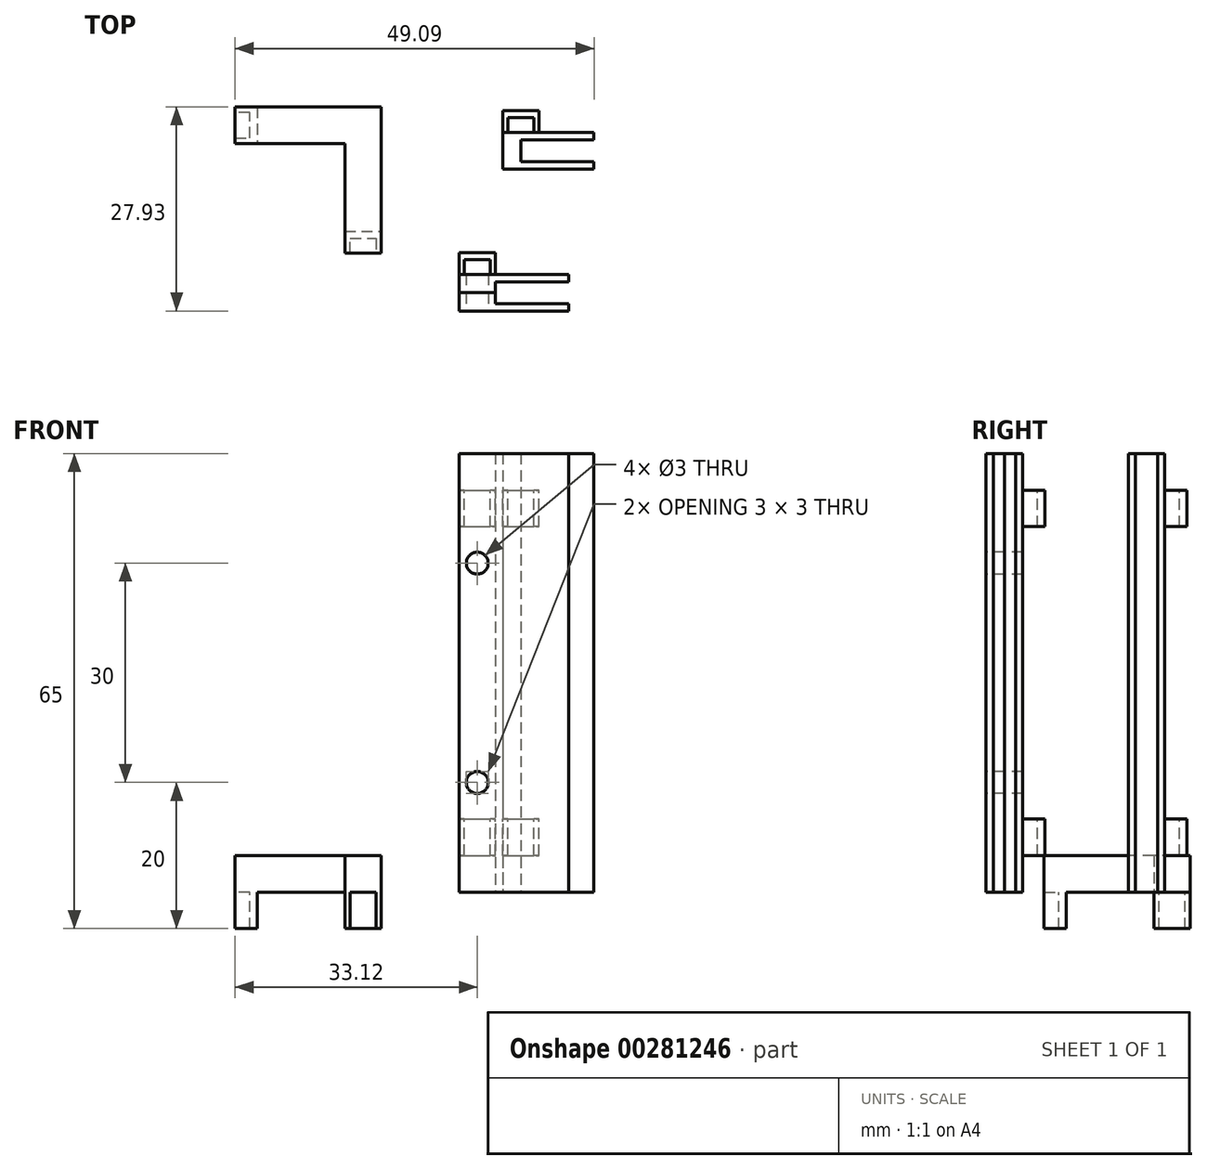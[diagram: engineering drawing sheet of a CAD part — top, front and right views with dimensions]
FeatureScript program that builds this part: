
annotation { "Feature Type Name" : "Feature", "Feature Type Description" : "" }
export const myFeature = defineFeature(function(context is Context, id is Id, definition is map)
    precondition{}
    {
        {
            var Q0;
            Q0=qCreatedBy(makeId("Top.planeOp"),FACE);
            var sketch = newSketch(context, id + "F0", { "sketchPlane" : qUnion([Q0])});
            skLineSegment(sketch, "E0.bottom", {"start": v(0, 0) * mm, "end": v(-10, 0) * mm});
            skLineSegment(sketch, "E0.top", {"start": v(0, 3) * mm, "end": v(-10, 3) * mm});
            skLineSegment(sketch, "E0.left", {"start": v(0, 0) * mm, "end": v(0, 3) * mm});
            skLineSegment(sketch, "E0.right", {"start": v(-10, 0) * mm, "end": v(-10, 3) * mm});
            skLineSegment(sketch, "E1.bottom", {"start": v(0, 0) * mm, "end": v(-15, 0) * mm});
            skLineSegment(sketch, "E1.top", {"start": v(0, -1) * mm, "end": v(-15, -1) * mm});
            skLineSegment(sketch, "E1.left", {"start": v(0, 0) * mm, "end": v(0, -1) * mm});
            skLineSegment(sketch, "E1.right", {"start": v(-15, 0) * mm, "end": v(-15, -1) * mm});
            skLineSegment(sketch, "E2.bottom", {"start": v(0, 3) * mm, "end": v(-15, 3) * mm});
            skLineSegment(sketch, "E2.top", {"start": v(0, 4) * mm, "end": v(-15, 4) * mm});
            skLineSegment(sketch, "E2.left", {"start": v(0, 3) * mm, "end": v(0, 4) * mm});
            skLineSegment(sketch, "E2.right", {"start": v(-15, 3) * mm, "end": v(-15, 4) * mm});
            skLineSegment(sketch, "E3", {"start": v(-15, 3) * mm, "end": v(-15, 0) * mm});
            skLineSegment(sketch, "E4", {"start": v(-15, 1.5) * mm, "end": v(-10, 1.5) * mm});
            skSolve(sketch);
        }
        {
            var Q0;
            Q0=makeQuery(id+"F0.imprint","IMPRINT",FACE,{"disambiguationData":[TD([[makeQuery(id+"F0.imprint","IMPRINT",EDGE,{"derivedFrom":sQuery(id+"F0.wireOp",EDGE,"E2.top")}),1.0]])]});
            var Q1;
            {var subQ3=sQuery(id+"F0.wireOp",EDGE,"E4");Q1=makeQuery(id+"F0.imprint","IMPRINT",FACE,{"disambiguationData":[TD([[makeQuery(id+"F0.imprint","IMPRINT",EDGE,{"derivedFrom":subQ3}),1.0]])]});}
            extrude(context, id + "F1", {"entities" : qUnion([Q0, Q1]), "depth" : 60 * mm});
        }
        {
            var Q0;
            {var subQ3=sQuery(id+"F0.wireOp",EDGE,"E4");Q0=makeQuery(id+"F0.imprint","IMPRINT",FACE,{"disambiguationData":[TD([[makeQuery(id+"F0.imprint","IMPRINT",EDGE,{"derivedFrom":subQ3}),-1.0]])]});}
            var Q1;
            Q1=makeQuery(id+"F0.imprint","IMPRINT",FACE,{"disambiguationData":[TD([[makeQuery(id+"F0.imprint","IMPRINT",EDGE,{"derivedFrom":sQuery(id+"F0.wireOp",EDGE,"E1.top")}),-1.0]])]});
            extrude(context, id + "F2", {"entities" : qUnion([Q0, Q1]), "depth" : 60 * mm});
        }
        {
            var Q0;
            Q0=makeQuery(id+"F2.opExtrude","SWEPT_FACE",FACE,{"disambiguationData":[OSD([sQuery(id+"F0.wireOp",EDGE,"E1.top")])]});
            var sketch = newSketch(context, id + "F3", { "sketchPlane" : qUnion([Q0])});
            skLineSegment(sketch, "E5.bottom", {"start": v(-15, 60) * mm, "end": v(-10, 60) * mm});
            skLineSegment(sketch, "E5.top", {"start": v(-15, 0) * mm, "end": v(-10, 0) * mm});
            skLineSegment(sketch, "E5.left", {"start": v(-15, 60) * mm, "end": v(-15, 0) * mm});
            skLineSegment(sketch, "E5.right", {"start": v(-10, 60) * mm, "end": v(-10, 0) * mm});
            skLineSegment(sketch, "E6.bottom", {"start": v(-15, 30) * mm, "end": v(-10, 30) * mm});
            skLineSegment(sketch, "E6.left", {"start": v(-15, 30) * mm, "end": v(-15, 60) * mm});
            skLineSegment(sketch, "E6.right", {"start": v(-10, 30) * mm, "end": v(-10, 60) * mm});
            skLineSegment(sketch, "E7.left", {"start": v(-15, 30) * mm, "end": v(-15, 0) * mm});
            skLineSegment(sketch, "E7.right", {"start": v(-10, 30) * mm, "end": v(-10, 0) * mm});
            skCircle(sketch, "E8", {"center": v(-12.5, 15) * mm, "radius": 1.5 * mm});
            skPoint(sketch, "E8.centerSnap0", {"position": v(-15, 15) * mm});
            skPoint(sketch, "E8.centerSnap1", {"position": v(-12.5, 30) * mm});
            skCircle(sketch, "E9", {"center": v(-12.5, 45) * mm, "radius": 1.5 * mm});
            skPoint(sketch, "E9.centerSnap0", {"position": v(-12.5, 60) * mm});
            skPoint(sketch, "E9.centerSnap1", {"position": v(-15, 45) * mm});
            skSolve(sketch);
        }
        {
            var Q0;
            Q0=sQuery(id+"F3.wireOp",VERTEX,"E9.center");
            var Q1;
            Q1=sQuery(id+"F3.wireOp",VERTEX,"E8.center");
            var Q2;
            Q2=makeQuery(id+"F1.opExtrude","SWEPT_BODY",BODY,{"disambiguationData":[OSD([sQuery(id+"F0.wireOp",EDGE,"E0.right"),sQuery(id+"F0.wireOp",EDGE,"E2.bottom"),sQuery(id+"F0.wireOp",EDGE,"E2.top"),sQuery(id+"F0.wireOp",EDGE,"E2.left"),sQuery(id+"F0.wireOp",EDGE,"E2.right"),sQuery(id+"F0.wireOp",EDGE,"E3"),sQuery(id+"F0.wireOp",EDGE,"E4")])]});
            var Q3;
            Q3=makeQuery(id+"F2.opExtrude","SWEPT_BODY",BODY,{"disambiguationData":[OSD([sQuery(id+"F0.wireOp",EDGE,"E0.right"),sQuery(id+"F0.wireOp",EDGE,"E1.bottom"),sQuery(id+"F0.wireOp",EDGE,"E1.top"),sQuery(id+"F0.wireOp",EDGE,"E1.left"),sQuery(id+"F0.wireOp",EDGE,"E1.right"),sQuery(id+"F0.wireOp",EDGE,"E3"),sQuery(id+"F0.wireOp",EDGE,"E4")])]});
            hole(context, id + "F4", {"style" : HoleStyle.SIMPLE, "endStyle" : HoleEndStyle.BLIND, "holeDiameter" : 3 * mm, "holeDepth" : 100 * mm, "tappedDepth" : 12 * mm, "tapClearance" : 3, "locations" : qUnion([Q0, Q1]), "scope" : qUnion([Q2, Q3])});
        }
        {
            var Q0;
            Q0=qCreatedBy(makeId("Top.planeOp"),FACE);
            var sketch = newSketch(context, id + "F5", { "sketchPlane" : qUnion([Q0])});
            skLineSegment(sketch, "E10.bottom", {"start": v(3.47, 22.43) * mm, "end": v(-6.53, 22.43) * mm});
            skLineSegment(sketch, "E10.top", {"start": v(3.47, 19.43) * mm, "end": v(-6.53, 19.43) * mm});
            skLineSegment(sketch, "E10.left", {"start": v(3.47, 22.43) * mm, "end": v(3.47, 19.43) * mm});
            skLineSegment(sketch, "E10.right", {"start": v(-6.53, 22.43) * mm, "end": v(-6.53, 19.43) * mm});
            skLineSegment(sketch, "E11.bottom", {"start": v(3.47, 20.93) * mm, "end": v(-9.03, 20.93) * mm});
            skLineSegment(sketch, "E11.top", {"start": v(3.47, 23.43) * mm, "end": v(-9.03, 23.43) * mm});
            skLineSegment(sketch, "E11.left", {"start": v(3.47, 20.93) * mm, "end": v(3.47, 23.43) * mm});
            skLineSegment(sketch, "E11.right", {"start": v(-9.03, 20.93) * mm, "end": v(-9.03, 23.43) * mm});
            skLineSegment(sketch, "E12.top", {"start": v(3.47, 18.43) * mm, "end": v(-9.03, 18.43) * mm});
            skLineSegment(sketch, "E12.left", {"start": v(3.47, 20.93) * mm, "end": v(3.47, 18.43) * mm});
            skLineSegment(sketch, "E12.right", {"start": v(-9.03, 20.93) * mm, "end": v(-9.03, 18.43) * mm});
            skSolve(sketch);
        }
        {
            var Q0;
            {var subQ1=sQuery(id+"F5.wireOp",EDGE,"E10.bottom");Q0=makeQuery(id+"F5.imprint","IMPRINT",FACE,{"disambiguationData":[TD([[makeQuery(id+"F5.imprint","IMPRINT",EDGE,{"derivedFrom":subQ1}),-1.0]])]});}
            var Q1;
            {var subQ5=sQuery(id+"F5.wireOp",EDGE,"E10.top");Q1=makeQuery(id+"F5.imprint","IMPRINT",FACE,{"disambiguationData":[TD([[makeQuery(id+"F5.imprint","IMPRINT",EDGE,{"derivedFrom":subQ5}),1.0]])]});}
            extrude(context, id + "F6", {"entities" : qUnion([Q0, Q1]), "depth" : 60 * mm});
        }
        {
            var Q0;
            Q0=makeQuery(id+"F1.opExtrude","CAP_FACE",FACE,{"disambiguationData":[OSD([sQuery(id+"F0.wireOp",EDGE,"E0.right"),sQuery(id+"F0.wireOp",EDGE,"E2.bottom"),sQuery(id+"F0.wireOp",EDGE,"E2.top"),sQuery(id+"F0.wireOp",EDGE,"E2.left"),sQuery(id+"F0.wireOp",EDGE,"E2.right"),sQuery(id+"F0.wireOp",EDGE,"E3"),sQuery(id+"F0.wireOp",EDGE,"E4")])],"isStart":false});
            var sketch = newSketch(context, id + "F7", { "sketchPlane" : qUnion([Q0])});
            skLineSegment(sketch, "E13", {"start": v(-15, 4) * mm, "end": v(-15, 7) * mm});
            skLineSegment(sketch, "E14", {"start": v(-15, 7) * mm, "end": v(-10, 7) * mm});
            skLineSegment(sketch, "E15", {"start": v(-10, 7) * mm, "end": v(-10, 4) * mm});
            skLineSegment(sketch, "E16", {"start": v(-10, 4) * mm, "end": v(-10.75, 4) * mm});
            skLineSegment(sketch, "E17", {"start": v(-15, 4) * mm, "end": v(-14.25, 4) * mm});
            skLineSegment(sketch, "E18", {"start": v(-14.25, 4) * mm, "end": v(-10.75, 4) * mm});
            skLineSegment(sketch, "E19", {"start": v(-10.75, 4) * mm, "end": v(-10.75, 6) * mm});
            skLineSegment(sketch, "E20", {"start": v(-14.25, 4) * mm, "end": v(-14.25, 6) * mm});
            skLineSegment(sketch, "E21", {"start": v(-14.25, 6) * mm, "end": v(-10.75, 6) * mm});
            skSolve(sketch);
        }
        {
            var Q0;
            Q0=makeQuery(id+"F7.imprint","IMPRINT",FACE,{"disambiguationData":[TD([[makeQuery(id+"F7.imprint","IMPRINT",EDGE,{"derivedFrom":sQuery(id+"F7.wireOp",EDGE,"E13")}),-1.0]])]});
            extrude(context, id + "F8", {"entities" : qUnion([Q0]), "operationType" : NewBodyOperationType.ADD, "oppositeDirection" : true, "depth" : 10 * mm, "hasSecondDirection" : true, "secondDirectionOppositeDirection" : true, "secondDirectionDepth" : 5 * mm});
        }
        {
            var Q0;
            Q0=makeQuery(id+"F7.imprint","IMPRINT",FACE,{"disambiguationData":[TD([[makeQuery(id+"F7.imprint","IMPRINT",EDGE,{"derivedFrom":sQuery(id+"F7.wireOp",EDGE,"E13")}),-1.0]])]});
            var Q1;
            Q1=makeQuery(id+"F1.opExtrude","CAP_FACE",FACE,{"disambiguationData":[OSD([sQuery(id+"F0.wireOp",EDGE,"E0.right"),sQuery(id+"F0.wireOp",EDGE,"E2.bottom"),sQuery(id+"F0.wireOp",EDGE,"E2.top"),sQuery(id+"F0.wireOp",EDGE,"E2.left"),sQuery(id+"F0.wireOp",EDGE,"E2.right"),sQuery(id+"F0.wireOp",EDGE,"E3"),sQuery(id+"F0.wireOp",EDGE,"E4")])],"isStart":true});
            extrude(context, id + "F9", {"entities" : qUnion([Q0]), "operationType" : NewBodyOperationType.ADD, "oppositeDirection" : true, "endBoundEntityFace" : qUnion([Q1]), "depth" : 55 * mm, "hasSecondDirection" : true, "secondDirectionOppositeDirection" : true, "secondDirectionDepth" : 50 * mm});
        }
        {
            var Q0;
            Q0=makeQuery(id+"F6.opExtrude","CAP_FACE",FACE,{"disambiguationData":[OSD([sQuery(id+"F5.wireOp",EDGE,"E10.bottom"),sQuery(id+"F5.wireOp",EDGE,"E10.top"),sQuery(id+"F5.wireOp",EDGE,"E10.right"),sQuery(id+"F5.wireOp",EDGE,"E11.top"),sQuery(id+"F5.wireOp",EDGE,"E11.left"),sQuery(id+"F5.wireOp",EDGE,"E11.right"),sQuery(id+"F5.wireOp",EDGE,"E12.top"),sQuery(id+"F5.wireOp",EDGE,"E12.left"),sQuery(id+"F5.wireOp",EDGE,"E12.right")])],"isStart":false});
            var sketch = newSketch(context, id + "F10", { "sketchPlane" : qUnion([Q0])});
            skLineSegment(sketch, "E22.bottom", {"start": v(-9.03, 23.43) * mm, "end": v(-4.03, 23.43) * mm});
            skLineSegment(sketch, "E22.top", {"start": v(-9.03, 26.43) * mm, "end": v(-4.03, 26.43) * mm});
            skLineSegment(sketch, "E22.left", {"start": v(-9.03, 23.43) * mm, "end": v(-9.03, 26.43) * mm});
            skLineSegment(sketch, "E22.right", {"start": v(-4.03, 23.43) * mm, "end": v(-4.03, 26.43) * mm});
            skLineSegment(sketch, "E23", {"start": v(-9.03, 23.43) * mm, "end": v(-8.28, 23.43) * mm});
            skLineSegment(sketch, "E24", {"start": v(-4.03, 23.43) * mm, "end": v(-4.78, 23.43) * mm});
            skLineSegment(sketch, "E25", {"start": v(-4.78, 23.43) * mm, "end": v(-8.28, 23.43) * mm});
            skLineSegment(sketch, "E26", {"start": v(-8.28, 23.43) * mm, "end": v(-8.28, 25.43) * mm});
            skLineSegment(sketch, "E27", {"start": v(-8.28, 25.43) * mm, "end": v(-4.78, 25.43) * mm});
            skLineSegment(sketch, "E28", {"start": v(-4.78, 25.43) * mm, "end": v(-4.78, 23.43) * mm});
            skSolve(sketch);
        }
        {
            var Q0;
            Q0=makeQuery(id+"F10.imprint","IMPRINT",FACE,{"disambiguationData":[TD([[makeQuery(id+"F10.imprint","IMPRINT",EDGE,{"derivedFrom":sQuery(id+"F10.wireOp",EDGE,"E22.top")}),-1.0]])]});
            extrude(context, id + "F11", {"entities" : qUnion([Q0]), "operationType" : NewBodyOperationType.ADD, "oppositeDirection" : true, "depth" : 10 * mm, "hasSecondDirection" : true, "secondDirectionOppositeDirection" : true, "secondDirectionDepth" : 5 * mm});
        }
        {
            var Q0;
            Q0=makeQuery(id+"F10.imprint","IMPRINT",FACE,{"disambiguationData":[TD([[makeQuery(id+"F10.imprint","IMPRINT",EDGE,{"derivedFrom":sQuery(id+"F10.wireOp",EDGE,"E22.top")}),-1.0]])]});
            extrude(context, id + "F12", {"entities" : qUnion([Q0]), "operationType" : NewBodyOperationType.ADD, "oppositeDirection" : true, "depth" : 55 * mm, "hasSecondDirection" : true, "secondDirectionOppositeDirection" : true, "secondDirectionDepth" : 50 * mm});
        }
        {
            var Q0;
            Q0=qCreatedBy(makeId("Top.planeOp"),FACE);
            var sketch = newSketch(context, id + "F13", { "sketchPlane" : qUnion([Q0])});
            skLineSegment(sketch, "E29.bottom", {"start": v(-30.62, 26.93) * mm, "end": v(-25.62, 26.93) * mm});
            skLineSegment(sketch, "E29.top", {"start": v(-30.62, 21.93) * mm, "end": v(-25.62, 21.93) * mm});
            skLineSegment(sketch, "E29.left", {"start": v(-30.62, 26.93) * mm, "end": v(-30.62, 21.93) * mm});
            skLineSegment(sketch, "E29.right", {"start": v(-25.62, 26.93) * mm, "end": v(-25.62, 21.93) * mm});
            skLineSegment(sketch, "E30.top", {"start": v(-30.62, 9.93) * mm, "end": v(-25.62, 9.93) * mm});
            skLineSegment(sketch, "E30.left", {"start": v(-30.62, 21.93) * mm, "end": v(-30.62, 9.93) * mm});
            skLineSegment(sketch, "E30.right", {"start": v(-25.62, 21.93) * mm, "end": v(-25.62, 9.93) * mm});
            skLineSegment(sketch, "E31.bottom", {"start": v(-30.62, 26.93) * mm, "end": v(-42.62, 26.93) * mm});
            skLineSegment(sketch, "E31.top", {"start": v(-30.62, 21.93) * mm, "end": v(-42.62, 21.93) * mm});
            skLineSegment(sketch, "E31.right", {"start": v(-42.62, 26.93) * mm, "end": v(-42.62, 21.93) * mm});
            skLineSegment(sketch, "E32.top", {"start": v(-30.62, 6.93) * mm, "end": v(-25.62, 6.93) * mm});
            skLineSegment(sketch, "E32.left", {"start": v(-30.62, 9.93) * mm, "end": v(-30.62, 6.93) * mm});
            skLineSegment(sketch, "E32.right", {"start": v(-25.62, 9.93) * mm, "end": v(-25.62, 6.93) * mm});
            skLineSegment(sketch, "E33.bottom", {"start": v(-42.62, 26.93) * mm, "end": v(-45.62, 26.93) * mm});
            skLineSegment(sketch, "E33.top", {"start": v(-42.62, 21.93) * mm, "end": v(-45.62, 21.93) * mm});
            skLineSegment(sketch, "E33.right", {"start": v(-45.62, 26.93) * mm, "end": v(-45.62, 21.93) * mm});
            skLineSegment(sketch, "E34", {"start": v(-45.62, 26.93) * mm, "end": v(-45.62, 26.18) * mm});
            skLineSegment(sketch, "E35", {"start": v(-45.62, 21.93) * mm, "end": v(-45.62, 22.68) * mm});
            skLineSegment(sketch, "E36", {"start": v(-45.62, 22.68) * mm, "end": v(-43.62, 22.68) * mm});
            skLineSegment(sketch, "E37", {"start": v(-43.62, 22.68) * mm, "end": v(-43.62, 26.18) * mm});
            skLineSegment(sketch, "E38", {"start": v(-43.62, 26.18) * mm, "end": v(-45.62, 26.18) * mm});
            skLineSegment(sketch, "E39", {"start": v(-30.62, 6.93) * mm, "end": v(-29.87, 6.93) * mm});
            skLineSegment(sketch, "E40", {"start": v(-29.87, 6.93) * mm, "end": v(-29.87, 8.93) * mm});
            skLineSegment(sketch, "E41", {"start": v(-29.87, 8.93) * mm, "end": v(-26.37, 8.93) * mm});
            skLineSegment(sketch, "E42", {"start": v(-26.37, 8.93) * mm, "end": v(-26.37, 6.93) * mm});
            skLineSegment(sketch, "E43", {"start": v(-26.37, 6.93) * mm, "end": v(-25.62, 6.93) * mm});
            skSolve(sketch);
        }
        {
            var Q0;
            Q0 = qSketchRegion(id + "F13", true);
            extrude(context, id + "F14", {"entities" : qUnion([Q0]), "depth" : 5 * mm});
        }
        {
            var Q0;
            Q0=makeQuery(id+"F13.imprint","IMPRINT",FACE,{"disambiguationData":[TD([[makeQuery(id+"F13.imprint","IMPRINT",EDGE,{"derivedFrom":sQuery(id+"F13.wireOp",EDGE,"E32.top")}),1.0]])]});
            var Q1;
            Q1=makeQuery(id+"F13.imprint","IMPRINT",FACE,{"disambiguationData":[TD([[makeQuery(id+"F13.imprint","IMPRINT",EDGE,{"derivedFrom":sQuery(id+"F13.wireOp",EDGE,"E33.right")}),1.0]])]});
            extrude(context, id + "F15", {"entities" : qUnion([Q0, Q1]), "operationType" : NewBodyOperationType.ADD, "oppositeDirection" : true, "depth" : 5 * mm});
        }
    });
